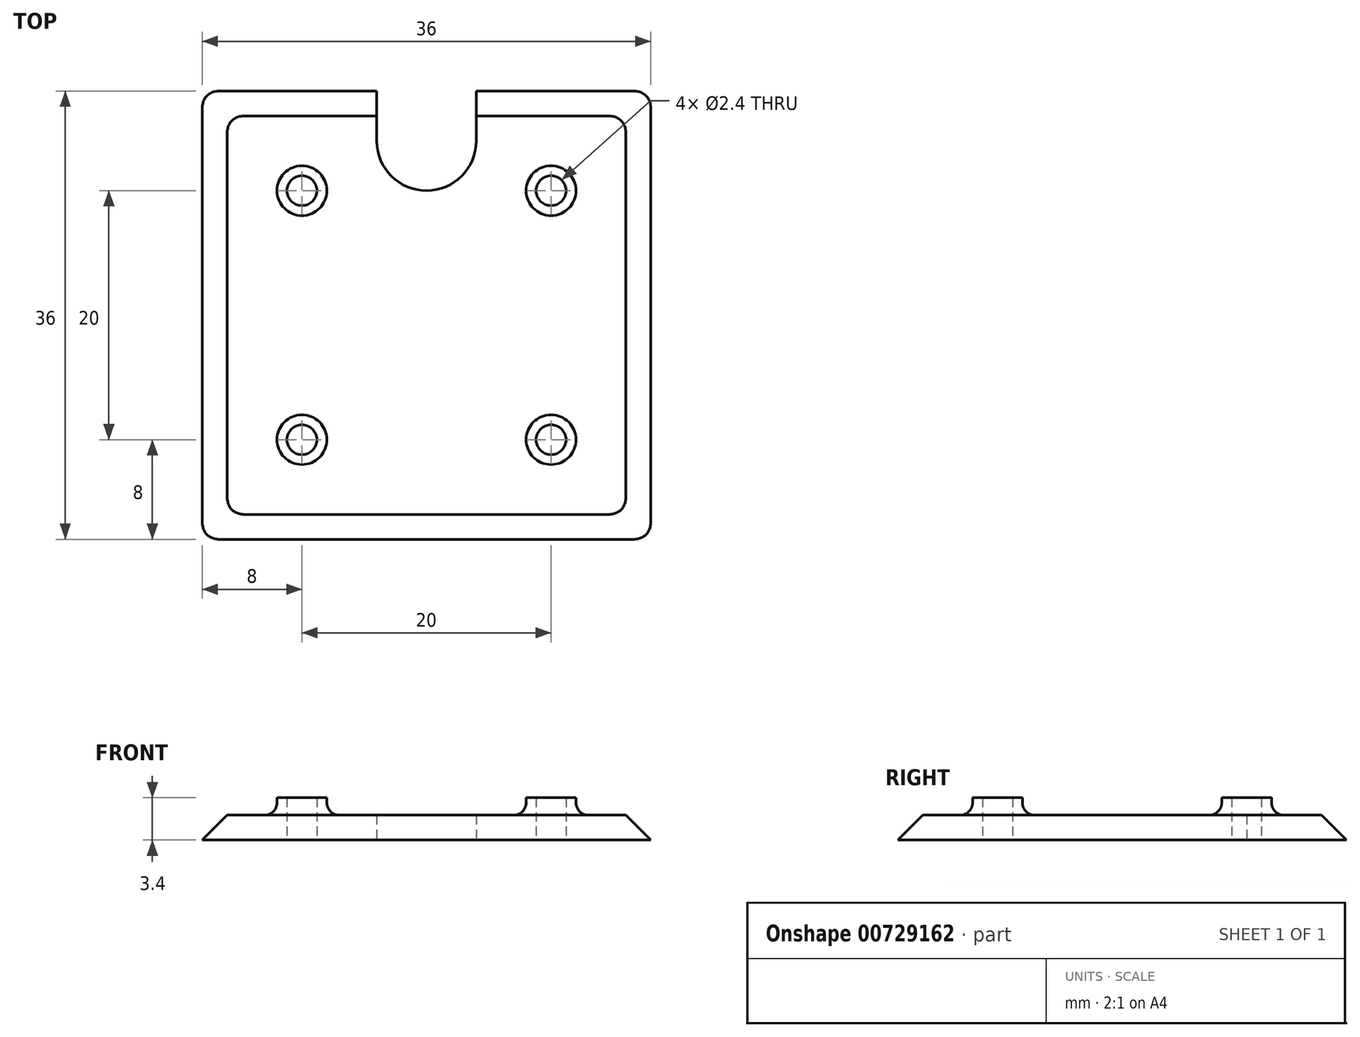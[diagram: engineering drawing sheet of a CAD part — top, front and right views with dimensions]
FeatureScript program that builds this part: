
annotation { "Feature Type Name" : "Feature", "Feature Type Description" : "" }
export const myFeature = defineFeature(function(context is Context, id is Id, definition is map)
    precondition{}
    {
        {
            var Q0;
            Q0=qCreatedBy(makeId("Top.planeOp"),FACE);
            var sketch = newSketch(context, id + "F0", { "sketchPlane" : qUnion([Q0])});
            skLineSegment(sketch, "E0.bottom", {"start": v(16, 16) * mm, "end": v(-16, 16) * mm});
            skLineSegment(sketch, "E0.top", {"start": v(16, -16) * mm, "end": v(-16, -16) * mm});
            skLineSegment(sketch, "E0.left", {"start": v(16, 16) * mm, "end": v(16, -16) * mm});
            skLineSegment(sketch, "E0.right", {"start": v(-16, 16) * mm, "end": v(-16, -16) * mm});
            skPoint(sketch, "E0.middle", {"position": v(0, 0) * mm});
            skSolve(sketch);
        }
        {
            var Q0;
            Q0=makeQuery(id+"F0.imprint","IMPRINT",FACE,{"disambiguationData":[TD([[makeQuery(id+"F0.imprint","IMPRINT",EDGE,{"derivedFrom":sQuery(id+"F0.wireOp",EDGE,"E0.bottom")}),1.0]])]});
            extrude(context, id + "F1", {"entities" : qUnion([Q0]), "oppositeDirection" : true, "depth" : 2 * mm, "offsetDistance" : 25 * mm, "hasDraft" : true, "draftAngle" : 45 * degree});
        }
        {
            var Q0;
            Q0=makeQuery(id+"F1.opExtrude","CAP_FACE",FACE,{"disambiguationData":[OSD([sQuery(id+"F0.wireOp",EDGE,"E0.bottom"),sQuery(id+"F0.wireOp",EDGE,"E0.top"),sQuery(id+"F0.wireOp",EDGE,"E0.left"),sQuery(id+"F0.wireOp",EDGE,"E0.right")])],"isStart":false});
            var sketch = newSketch(context, id + "F2", { "sketchPlane" : qUnion([Q0])});
            skLineSegment(sketch, "E1.bottom", {"start": v(10, 10) * mm, "end": v(-10, 10) * mm, "construction": true});
            skLineSegment(sketch, "E1.top", {"start": v(10, -10) * mm, "end": v(-10, -10) * mm, "construction": true});
            skLineSegment(sketch, "E1.left", {"start": v(10, 10) * mm, "end": v(10, -10) * mm, "construction": true});
            skLineSegment(sketch, "E1.right", {"start": v(-10, 10) * mm, "end": v(-10, -10) * mm, "construction": true});
            skPoint(sketch, "E1.middle", {"position": v(0, 0) * mm});
            skCircle(sketch, "E2", {"center": v(-10, 10) * mm, "radius": 2 * mm});
            skCircle(sketch, "E3.1.0", {"center": v(-10, -10) * mm, "radius": 2 * mm});
            skCircle(sketch, "E3.2.0", {"center": v(10, -10) * mm, "radius": 2 * mm});
            skCircle(sketch, "E3.3.0", {"center": v(10, 10) * mm, "radius": 2 * mm});
            skSolve(sketch);
        }
        {
            var Q0;
            Q0=makeQuery(id+"F2.imprint","IMPRINT",FACE,{"disambiguationData":[TD([[makeQuery(id+"F2.imprint","IMPRINT",EDGE,{"derivedFrom":sQuery(id+"F2.wireOp",EDGE,"E2")}),1.0]])]});
            var Q1;
            Q1=makeQuery(id+"F2.imprint","IMPRINT",FACE,{"disambiguationData":[TD([[makeQuery(id+"F2.imprint","IMPRINT",EDGE,{"derivedFrom":sQuery(id+"F2.wireOp",EDGE,"E3.3.0")}),1.0]])]});
            var Q2;
            Q2=makeQuery(id+"F2.imprint","IMPRINT",FACE,{"disambiguationData":[TD([[makeQuery(id+"F2.imprint","IMPRINT",EDGE,{"derivedFrom":sQuery(id+"F2.wireOp",EDGE,"E3.2.0")}),1.0]])]});
            var Q3;
            Q3=makeQuery(id+"F2.imprint","IMPRINT",FACE,{"disambiguationData":[TD([[makeQuery(id+"F2.imprint","IMPRINT",EDGE,{"derivedFrom":sQuery(id+"F2.wireOp",EDGE,"E3.1.0")}),1.0]])]});
            extrude(context, id + "F3", {"entities" : qUnion([Q0, Q1, Q2, Q3]), "operationType" : NewBodyOperationType.ADD, "oppositeDirection" : true, "depth" : 3.4 * mm, "offsetDistance" : 25 * mm});
        }
        {
            var Q0;
            Q0=sQuery(id+"F2.wireOp",VERTEX,"E1.bottom.end");
            var Q1;
            Q1=sQuery(id+"F2.wireOp",VERTEX,"E1.bottom.start");
            var Q2;
            Q2=sQuery(id+"F2.wireOp",VERTEX,"E1.top.start");
            var Q3;
            Q3=sQuery(id+"F2.wireOp",VERTEX,"E1.top.end");
            var Q4;
            Q4=makeQuery(id+"F1.opExtrude","SWEPT_BODY",BODY,{"disambiguationData":[OSD([sQuery(id+"F0.wireOp",EDGE,"E0.bottom"),sQuery(id+"F0.wireOp",EDGE,"E0.top"),sQuery(id+"F0.wireOp",EDGE,"E0.left"),sQuery(id+"F0.wireOp",EDGE,"E0.right")])]});
            hole(context, id + "F4", {"style" : HoleStyle.SIMPLE, "endStyle" : HoleEndStyle.THROUGH, "holeDiameter" : 2.4 * mm, "majorDiameter" : 5 * mm, "isTappedThrough" : true, "tappedDepth" : 12 * mm, "tapClearance" : 3, "locations" : qUnion([Q0, Q1, Q2, Q3]), "scope" : qUnion([Q4])});
        }
        {
            var Q0;
            Q0=makeQuery(id+"F2.imprint","IMPRINT",FACE,{"disambiguationData":[TD([[makeQuery(id+"F2.imprint","IMPRINT",EDGE,{"derivedFrom":sQuery(id+"F2.wireOp",EDGE,"E2")}),-1.0]])]});
            var sketch = newSketch(context, id + "F5", { "sketchPlane" : qUnion([Q0])});
            skLineSegment(sketch, "E4.0", {"start": v(18, -18) * mm, "end": v(-18, -18) * mm, "construction": true});
            skLineSegment(sketch, "E5", {"start": v(-4, -18) * mm, "end": v(-4, -14) * mm});
            skArc(sketch, "E6", {"start": v(4, -14) * mm, "mid": v(0, -10) * mm, "end": v(-4, -14) * mm});
            skPoint(sketch, "E6.centerSnap0", {"position": v(0, -18) * mm});
            skLineSegment(sketch, "E7", {"start": v(4, -18) * mm, "end": v(4, -14) * mm});
            skLineSegment(sketch, "E8", {"start": v(-4, -18) * mm, "end": v(4, -18) * mm});
            skSolve(sketch);
        }
        {
            var Q0;
            Q0 = qSketchRegion(id + "F5", true);
            extrude(context, id + "F6", {"entities" : qUnion([Q0]), "operationType" : NewBodyOperationType.REMOVE, "endBound" : BoundingType.THROUGH_ALL, "oppositeDirection" : true, "depth" : 25 * mm, "offsetDistance" : 25 * mm});
        }
        {
            var Q0;
            Q0=makeQuery(id+"F1.opExtrude","SWEPT_EDGE",EDGE,{"disambiguationData":[OSD([sQuery(id+"F0.wireOp",EDGE,"E0.top"),sQuery(id+"F0.wireOp",EDGE,"E0.right")])]});
            var Q1;
            Q1=makeQuery(id+"F1.opExtrude","SWEPT_EDGE",EDGE,{"disambiguationData":[OSD([sQuery(id+"F0.wireOp",EDGE,"E0.top"),sQuery(id+"F0.wireOp",EDGE,"E0.left")])]});
            var Q2;
            Q2=makeQuery(id+"F1.opExtrude","SWEPT_EDGE",EDGE,{"disambiguationData":[OSD([sQuery(id+"F0.wireOp",EDGE,"E0.bottom"),sQuery(id+"F0.wireOp",EDGE,"E0.left")])]});
            var Q3;
            Q3=makeQuery(id+"F1.opExtrude","SWEPT_EDGE",EDGE,{"disambiguationData":[OSD([sQuery(id+"F0.wireOp",EDGE,"E0.bottom"),sQuery(id+"F0.wireOp",EDGE,"E0.right")])]});
            fillet(context, id + "F7", {"entities" : qUnion([Q0, Q1, Q2, Q3]), "radius" : 2 * mm, "tangentPropagation" : true, "allowEdgeOverflow" : false});
        }
        {
            var Q0;
            Q0=makeQuery(id+"F3.boolean.opBoolean","INTERSECT",EDGE,{"derivedFrom":[makeQuery(id+"F1.opExtrude","CAP_FACE",FACE,{"disambiguationData":[OSD([sQuery(id+"F0.wireOp",EDGE,"E0.bottom"),sQuery(id+"F0.wireOp",EDGE,"E0.top"),sQuery(id+"F0.wireOp",EDGE,"E0.left"),sQuery(id+"F0.wireOp",EDGE,"E0.right")])],"isStart":true}),makeQuery(id+"F3.opExtrude","SWEPT_FACE",FACE,{"disambiguationData":[OSD([sQuery(id+"F2.wireOp",EDGE,"E3.1.0")])]})]});
            var Q1;
            Q1=makeQuery(id+"F3.boolean.opBoolean","INTERSECT",EDGE,{"derivedFrom":[makeQuery(id+"F1.opExtrude","CAP_FACE",FACE,{"disambiguationData":[OSD([sQuery(id+"F0.wireOp",EDGE,"E0.bottom"),sQuery(id+"F0.wireOp",EDGE,"E0.top"),sQuery(id+"F0.wireOp",EDGE,"E0.left"),sQuery(id+"F0.wireOp",EDGE,"E0.right")])],"isStart":true}),makeQuery(id+"F3.opExtrude","SWEPT_FACE",FACE,{"disambiguationData":[OSD([sQuery(id+"F2.wireOp",EDGE,"E2")])]})]});
            var Q2;
            Q2=makeQuery(id+"F3.boolean.opBoolean","INTERSECT",EDGE,{"derivedFrom":[makeQuery(id+"F1.opExtrude","CAP_FACE",FACE,{"disambiguationData":[OSD([sQuery(id+"F0.wireOp",EDGE,"E0.bottom"),sQuery(id+"F0.wireOp",EDGE,"E0.top"),sQuery(id+"F0.wireOp",EDGE,"E0.left"),sQuery(id+"F0.wireOp",EDGE,"E0.right")])],"isStart":true}),makeQuery(id+"F3.opExtrude","SWEPT_FACE",FACE,{"disambiguationData":[OSD([sQuery(id+"F2.wireOp",EDGE,"E3.3.0")])]})]});
            var Q3;
            Q3=makeQuery(id+"F3.boolean.opBoolean","INTERSECT",EDGE,{"derivedFrom":[makeQuery(id+"F1.opExtrude","CAP_FACE",FACE,{"disambiguationData":[OSD([sQuery(id+"F0.wireOp",EDGE,"E0.bottom"),sQuery(id+"F0.wireOp",EDGE,"E0.top"),sQuery(id+"F0.wireOp",EDGE,"E0.left"),sQuery(id+"F0.wireOp",EDGE,"E0.right")])],"isStart":true}),makeQuery(id+"F3.opExtrude","SWEPT_FACE",FACE,{"disambiguationData":[OSD([sQuery(id+"F2.wireOp",EDGE,"E3.2.0")])]})]});
            fillet(context, id + "F8", {"entities" : qUnion([Q0, Q1, Q2, Q3]), "radius" : 1 * mm, "tangentPropagation" : true, "allowEdgeOverflow" : false});
        }
    });
